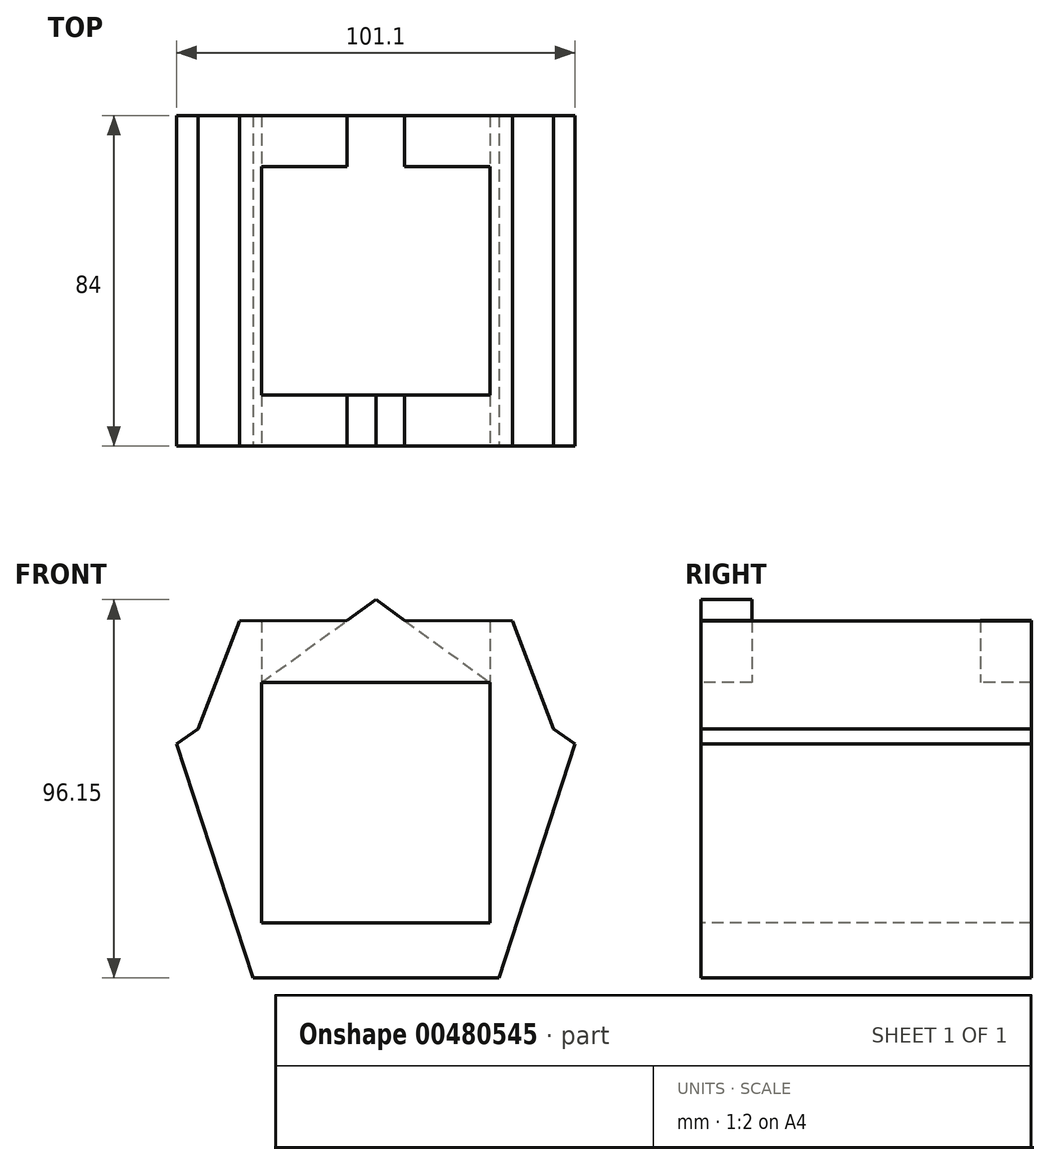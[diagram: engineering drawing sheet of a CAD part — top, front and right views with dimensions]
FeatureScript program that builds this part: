
annotation { "Feature Type Name" : "Feature", "Feature Type Description" : "" }
export const myFeature = defineFeature(function(context is Context, id is Id, definition is map)
    precondition{}
    {
        {
            var Q0;
            Q0=qCreatedBy(makeId("Front.planeOp"),FACE);
            var sketch = newSketch(context, id + "F0", { "sketchPlane" : qUnion([Q0])});
            skCircle(sketch, "E0.cCircle", {"center": v(0, 0) * mm, "radius": 43 * mm, "construction": true});
            skLineSegment(sketch, "E0.0", {"start": v(31.24, -43) * mm, "end": v(-31.24, -43) * mm});
            skLineSegment(sketch, "E0.1", {"start": v(-31.24, -43) * mm, "end": v(-50.55, 16.42) * mm});
            skLineSegment(sketch, "E0.2", {"start": v(-50.55, 16.42) * mm, "end": v(0, 53.15) * mm});
            skLineSegment(sketch, "E0.3", {"start": v(0, 53.15) * mm, "end": v(50.55, 16.42) * mm});
            skLineSegment(sketch, "E0.4", {"start": v(50.55, 16.42) * mm, "end": v(31.24, -43) * mm});
            skPoint(sketch, "E0.0.midPoint", {"position": v(0, -43) * mm});
            skLineSegment(sketch, "E1.bottom", {"start": v(29, 29) * mm, "end": v(-29, 29) * mm});
            skLineSegment(sketch, "E1.top", {"start": v(29, -29) * mm, "end": v(-29, -29) * mm});
            skLineSegment(sketch, "E1.left", {"start": v(29, 29) * mm, "end": v(29, -29) * mm});
            skLineSegment(sketch, "E1.right", {"start": v(-29, 29) * mm, "end": v(-29, -29) * mm});
            skLineSegment(sketch, "E2", {"start": v(-29, 29) * mm, "end": v(-29, 32.08) * mm});
            skLineSegment(sketch, "E3", {"start": v(29, 29) * mm, "end": v(29, 32.08) * mm});
            skLineSegment(sketch, "E4", {"start": v(-29, 32.08) * mm, "end": v(29, 32.08) * mm});
            skLineSegment(sketch, "E5", {"start": v(29, 32.08) * mm, "end": v(50.55, 16.42) * mm});
            skLineSegment(sketch, "E6", {"start": v(39.77, 24.25) * mm, "end": v(0, 53.15) * mm});
            skLineSegment(sketch, "E7", {"start": v(29, 32.08) * mm, "end": v(0, 53.15) * mm});
            skLineSegment(sketch, "E8", {"start": v(50.55, 16.42) * mm, "end": v(39.77, 24.25) * mm});
            skLineSegment(sketch, "E9", {"start": v(0, 53.15) * mm, "end": v(14.5, 42.62) * mm});
            skLineSegment(sketch, "E10", {"start": v(14.5, 42.62) * mm, "end": v(7.25, 47.88) * mm});
            skLineSegment(sketch, "E11", {"start": v(45.16, 20.34) * mm, "end": v(34.67, 47.71) * mm});
            skLineSegment(sketch, "E12", {"start": v(34.67, 47.71) * mm, "end": v(7.25, 47.88) * mm});
            skLineSegment(sketch, "E13.MirrorCS", {"start": v(-34.67, 47.71) * mm, "end": v(-7.25, 47.88) * mm});
            skLineSegment(sketch, "E14.MirrorCS", {"start": v(-45.16, 20.34) * mm, "end": v(-34.67, 47.71) * mm});
            skSolve(sketch);
        }
        {
            var Q0;
            Q0 = qSketchRegion(id + "F0", true);
            extrude(context, id + "F1", {"entities" : qUnion([Q0]), "oppositeDirection" : true, "depth" : 42 * mm, "hasSecondDirection" : true, "secondDirectionOppositeDirection" : false, "secondDirectionDepth" : 42 * mm});
        }
        {
            var Q0;
            Q0 = qSketchRegion(id + "F0", true);
            extrude(context, id + "F2", {"entities" : qUnion([Q0]), "operationType" : NewBodyOperationType.ADD, "depth" : 25 * mm});
        }
        {
            var Q0;
            Q0=makeQuery(id+"F1.opExtrude","SWEPT_FACE",FACE,{"disambiguationData":[OSD([sQuery(id+"F0.wireOp",EDGE,"E0.0")])]});
            var sketch = newSketch(context, id + "F3", { "sketchPlane" : qUnion([Q0])});
            skLineSegment(sketch, "E15.bottom", {"start": v(-29, 29) * mm, "end": v(29, 29) * mm});
            skLineSegment(sketch, "E15.top", {"start": v(-29, -29) * mm, "end": v(29, -29) * mm});
            skLineSegment(sketch, "E15.left", {"start": v(-29, 29) * mm, "end": v(-29, -29) * mm});
            skLineSegment(sketch, "E15.right", {"start": v(29, 29) * mm, "end": v(29, -29) * mm});
            skPoint(sketch, "E15.middle", {"position": v(0, 0) * mm});
            skLineSegment(sketch, "E16", {"start": v(-29, 29) * mm, "end": v(-31.24, 29) * mm});
            skLineSegment(sketch, "E17", {"start": v(-31.24, 29) * mm, "end": v(-31.24, -29) * mm});
            skLineSegment(sketch, "E18", {"start": v(-31.24, -29) * mm, "end": v(-29, -29) * mm});
            skLineSegment(sketch, "E19", {"start": v(29, -29) * mm, "end": v(31.24, -29) * mm});
            skLineSegment(sketch, "E20", {"start": v(31.24, -29) * mm, "end": v(31.24, 29) * mm});
            skLineSegment(sketch, "E21", {"start": v(31.24, 29) * mm, "end": v(29, 29) * mm});
            skLineSegment(sketch, "E22", {"start": v(-29, 29) * mm, "end": v(-35, 29) * mm});
            skLineSegment(sketch, "E23", {"start": v(-35, 29) * mm, "end": v(-35, -29) * mm});
            skLineSegment(sketch, "E24", {"start": v(-35, -29) * mm, "end": v(-29, -29) * mm});
            skLineSegment(sketch, "E25.MirrorCS", {"start": v(35, 29) * mm, "end": v(35, -29) * mm});
            skLineSegment(sketch, "E26.MirrorCS", {"start": v(29, 29) * mm, "end": v(35, 29) * mm});
            skLineSegment(sketch, "E27.MirrorCS", {"start": v(35, -29) * mm, "end": v(29, -29) * mm});
            skSolve(sketch);
        }
        {
            var Q0;
            {var subQ3=sQuery(id+"F0.wireOp",EDGE,"E4");Q0=makeQuery(id+"F0.imprint","IMPRINT",FACE,{"disambiguationData":[TD([[makeQuery(id+"F0.imprint","IMPRINT",EDGE,{"derivedFrom":subQ3}),1.0]])]});}
            extrude(context, id + "F4", {"entities" : qUnion([Q0]), "operationType" : NewBodyOperationType.REMOVE, "oppositeDirection" : true, "depth" : 65.4 * mm});
        }
        {
            var Q0;
            Q0=makeQuery(id+"F3.imprint","IMPRINT",FACE,{"disambiguationData":[TD([[makeQuery(id+"F3.imprint","IMPRINT",EDGE,{"derivedFrom":sQuery(id+"F3.wireOp",EDGE,"E15.bottom")}),-1.0]])]});
            extrude(context, id + "F5", {"entities" : qUnion([Q0]), "operationType" : NewBodyOperationType.REMOVE, "oppositeDirection" : true, "depth" : 107 * mm, "hasSecondDirection" : true, "secondDirectionOppositeDirection" : true, "secondDirectionDepth" : 31.4 * mm});
        }
        {
            var Q0;
            {var subQ0=sQuery(id+"F3.wireOp",EDGE,"E15.left");Q0=makeQuery(id+"F3.imprint","IMPRINT",FACE,{"disambiguationData":[TD([[makeQuery(id+"F3.imprint","IMPRINT",EDGE,{"derivedFrom":subQ0}),-1.0]])]});}
            var Q1;
            {var subQ0=sQuery(id+"F3.wireOp",EDGE,"E17");Q1=makeQuery(id+"F3.imprint","IMPRINT",FACE,{"disambiguationData":[TD([[makeQuery(id+"F3.imprint","IMPRINT",EDGE,{"derivedFrom":subQ0}),1.0]])]});}
            var Q2;
            {var subQ0=sQuery(id+"F3.wireOp",EDGE,"E15.right");Q2=makeQuery(id+"F3.imprint","IMPRINT",FACE,{"disambiguationData":[TD([[makeQuery(id+"F3.imprint","IMPRINT",EDGE,{"derivedFrom":subQ0}),1.0]])]});}
            var Q3;
            {var subQ0=sQuery(id+"F3.wireOp",EDGE,"E20");Q3=makeQuery(id+"F3.imprint","IMPRINT",FACE,{"disambiguationData":[TD([[makeQuery(id+"F3.imprint","IMPRINT",EDGE,{"derivedFrom":subQ0}),-1.0]])]});}
            extrude(context, id + "F6", {"entities" : qUnion([Q0, Q1, Q2, Q3]), "operationType" : NewBodyOperationType.ADD, "oppositeDirection" : true, "depth" : 78 * mm, "hasSecondDirection" : true, "secondDirectionOppositeDirection" : true, "secondDirectionDepth" : 25 * mm});
        }
    });
